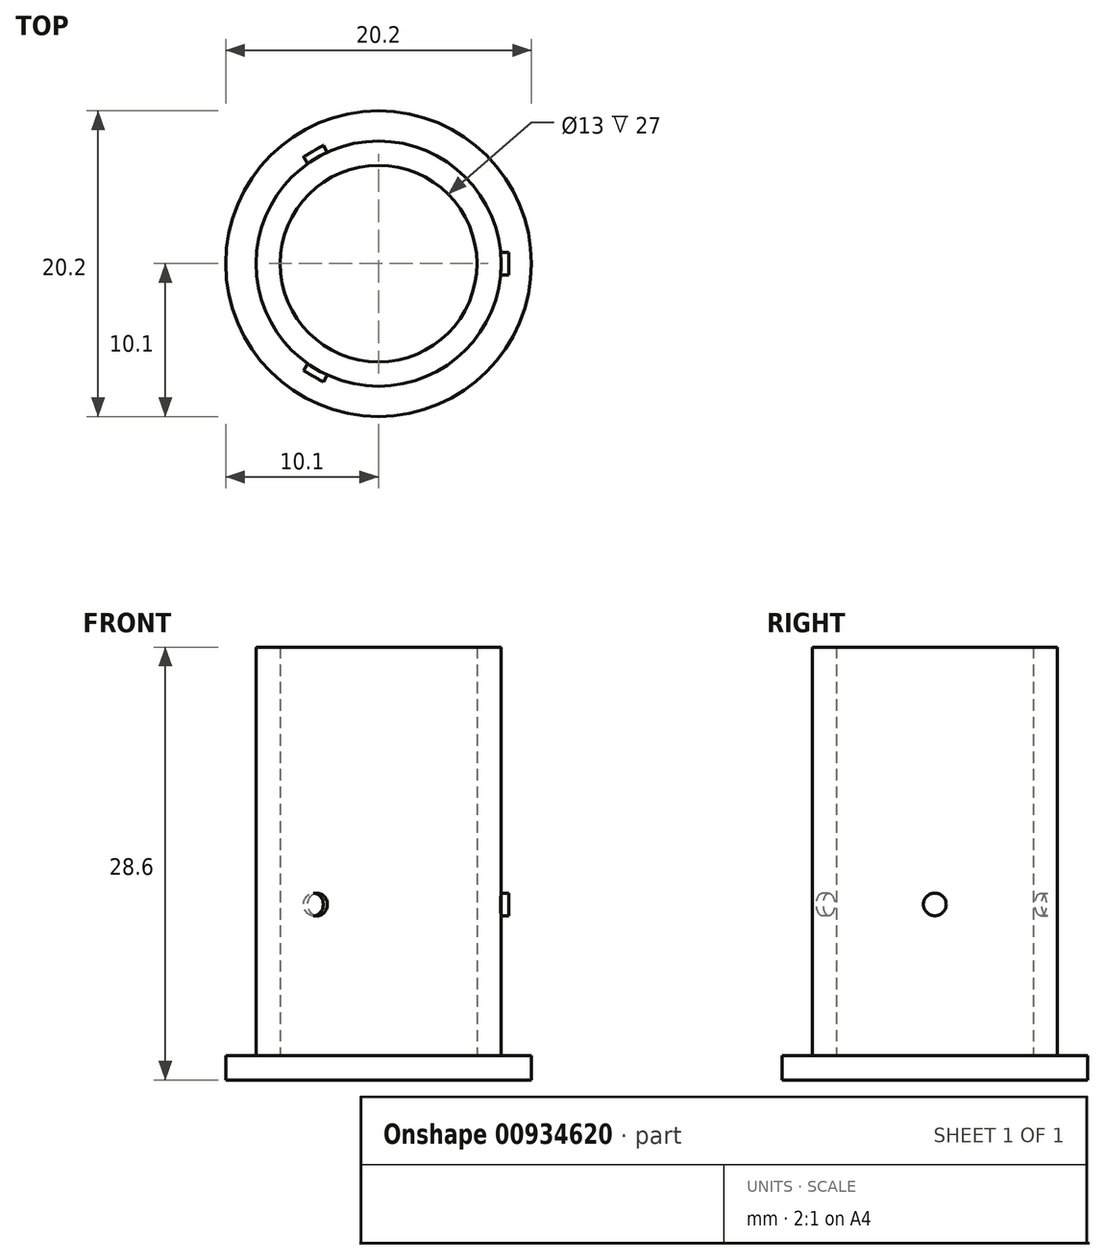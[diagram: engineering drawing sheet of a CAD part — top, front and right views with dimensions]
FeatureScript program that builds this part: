
annotation { "Feature Type Name" : "Feature", "Feature Type Description" : "" }
export const myFeature = defineFeature(function(context is Context, id is Id, definition is map)
    precondition{}
    {
        {
            var Q0;
            Q0=qCreatedBy(makeId("Right.planeOp"),FACE);
            cPlane(context, id + "F0", {"entities" : qUnion([Q0]), "cplaneType" : CPlaneType.OFFSET, "offset" : 8.6 * mm, "width" : 150 * mm, "height" : 150 * mm});
        }
        {
            var Q0;
            Q0=qCreatedBy(makeId("Front.planeOp"),FACE);
            var sketch = newSketch(context, id + "F1", { "sketchPlane" : qUnion([Q0])});
            skLineSegment(sketch, "E0", {"start": v(0, 0) * mm, "end": v(-6.5, 0) * mm});
            skLineSegment(sketch, "E1", {"start": v(-6.5, 0) * mm, "end": v(-6.5, 27) * mm});
            skLineSegment(sketch, "E2", {"start": v(-6.5, 27) * mm, "end": v(-8.1, 27) * mm});
            skLineSegment(sketch, "E3", {"start": v(-8.1, 27) * mm, "end": v(-8.1, 0) * mm});
            skLineSegment(sketch, "E4", {"start": v(-8.1, 0) * mm, "end": v(-10.1, 0) * mm});
            skLineSegment(sketch, "E5", {"start": v(-10.1, 0) * mm, "end": v(-10.1, -1.6) * mm});
            skLineSegment(sketch, "E6", {"start": v(-10.1, -1.6) * mm, "end": v(0, -1.6) * mm});
            skLineSegment(sketch, "E7", {"start": v(0, -1.6) * mm, "end": v(0, 0) * mm});
            skSolve(sketch);
        }
        {
            var Q0;
            Q0=makeQuery(id+"F1.imprint","IMPRINT",FACE,{"disambiguationData":[TD([[makeQuery(id+"F1.imprint","IMPRINT",EDGE,{"derivedFrom":sQuery(id+"F1.wireOp",EDGE,"E0")}),1.0]])]});
            var Q1;
            Q1=sQuery(id+"F1.wireOp",EDGE,"E7");
            revolve(context, id + "F2", {"surfaceOperationType" : NewSurfaceOperationType.NEW, "entities" : qUnion([Q0]), "axis" : qUnion([Q1]), "revolveType" : RevolveType.FULL});
        }
        {
            var Q0;
            Q0=qCreatedBy(id+"F0.planeOp",FACE);
            var sketch = newSketch(context, id + "F3", { "sketchPlane" : qUnion([Q0])});
            skCircle(sketch, "E8", {"center": v(0, 10) * mm, "radius": 0.75 * mm});
            skSolve(sketch);
        }
        {
            var Q0;
            Q0=makeQuery(id+"F3.imprint","IMPRINT",FACE,{"disambiguationData":[TD([[makeQuery(id+"F3.imprint","IMPRINT",EDGE,{"derivedFrom":sQuery(id+"F3.wireOp",EDGE,"E8")}),1.0]])]});
            var Q1;
            Q1=makeQuery(id+"F2.opRevolve","SWEPT_BODY",BODY,{"disambiguationData":[OSD([sQuery(id+"F1.wireOp",EDGE,"E0"),sQuery(id+"F1.wireOp",EDGE,"E1"),sQuery(id+"F1.wireOp",EDGE,"E2"),sQuery(id+"F1.wireOp",EDGE,"E3"),sQuery(id+"F1.wireOp",EDGE,"E4"),sQuery(id+"F1.wireOp",EDGE,"E5"),sQuery(id+"F1.wireOp",EDGE,"E6"),sQuery(id+"F1.wireOp",EDGE,"E7")])]});
            extrude(context, id + "F4", {"entities" : qUnion([Q0]), "endBound" : BoundingType.UP_TO_BODY, "oppositeDirection" : true, "depth" : 25 * mm, "endBoundEntityBody" : qUnion([Q1]), "offsetDistance" : 25 * mm});
        }
        {
            var Q0;
            Q0=makeQuery(id+"F4.opExtrude","SWEPT_BODY",BODY,{"disambiguationData":[OSD([sQuery(id+"F3.wireOp",EDGE,"E8")])]});
            var Q1;
            Q1=sQuery(id+"F1.wireOp",EDGE,"E7");
            circularPattern(context, id + "F5", {"entities" : qUnion([Q0]), "axis" : qUnion([Q1]), "angle" : 360 * degree, "instanceCount" : 3, "equalSpace" : true});
        }
    });
